# Revit family: KingswayGroup_SpDspnsrs_Anti-LigatureManualSoapDispenser
name_source: partatom
category: Specialty Equipment
units: mm (PartAtom-declared; Revit-internal decimal feet)

## family parameters
Always vertical = Yes
Cut with Voids When Loaded = No
Part Type = Normal
Room Calculation Point = No
Round Connector Dimension = Use Diameter
Shared = No
Work Plane-Based = No

## types (1)
- KingswayGroup_SpDspnsrs_Anti-LigatureManualSoapDispenser
    AssetType = Fixed
    BIMObjectName = KingswayGroup_SoapDispensers_Anti-LigatureManualSoapDispenser
    Category = Pr_40_70_22_81:Soap dispensers
    Color = For full range of available finishes and colours, contact Kingsway Group
    Default Elevation = 0 mm  [stored 0 ft]
    Description = Manual Soap Dispenser
    DispenserMaterial = NBS_Concept
    DurationUnit = year
    Features = A surface-mounted Anti-Ligature Soap Dispenser with a refillable soap reservoir to provide a hygienic, safe, and durable solution to hand sanitisation in patient accessible washrooms. The KG07 Anti-Ligature Soap Dispenser uses a refillable dispensing unit (1000ml capacity) which can be refilled with liquid soap. Liquid soap is dispensed from the unit by pressing the anti-ligature button on the front side.
    Finish = For full range of available finishes and colours, contact Kingsway Group
    Grade = 316
    Manufacturer = Kingsway Group
    ManufacturerName = Kingsway Group
    ManufacturerURL = https://kingswaygroupglobal.com
    Material = Stainless Steel
    Model = KG07
    ModelNumber = KG07
    ModelReference = Anti-Ligature Manual Soap Dispenser
    Name = SoapDispensers_Anti-LigatureManualSoapDispenser_KG07_KingswayGroup
    NominalHeight = 445 mm  [stored 1.45997 ft]
    NominalLength = 165 mm
    NominalWidth = 110 mm  [stored 0.360892 ft]
    ProductInformation = https://kingswaygroupglobal.com
    Size = 165 x 445 x 110 mm
    URL = https://kingswaygroupglobal.com
    Uniclass2015Code = Pr_40_70_22_81
    Uniclass2015Title = Soap dispensers
    Uniclass2015Version = Products v1.36
    Version = 1
    WarrantyDescription = 5-Year Guarantee *For faulty manufacture and not for damage
    WarrantyDurationParts = 5
    WarrantyDurationUnit = year

note: [stored X ft] marks values corroborated as IEEE doubles in the binary element streams (Revit-internal decimal feet)

## geometry (parser evidence)
native form markers: Sweep x2
no freeform markers — native parametric forms only
